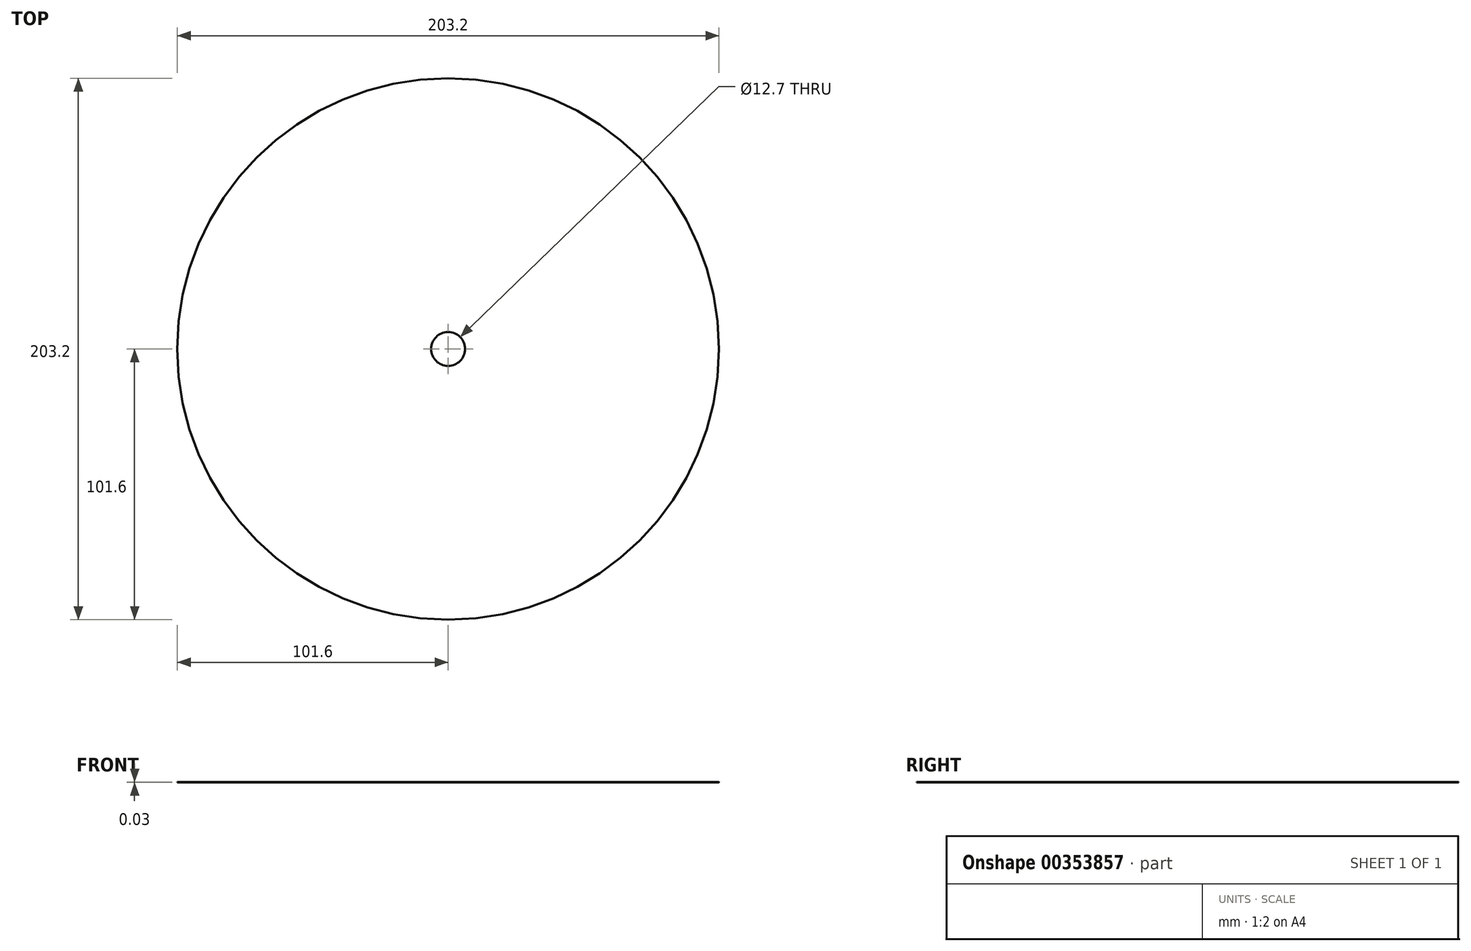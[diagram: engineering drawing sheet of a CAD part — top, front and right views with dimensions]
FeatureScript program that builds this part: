
annotation { "Feature Type Name" : "Feature", "Feature Type Description" : "" }
export const myFeature = defineFeature(function(context is Context, id is Id, definition is map)
    precondition{}
    {
        {
            var Q0;
            Q0=qCreatedBy(makeId("Top.planeOp"),FACE);
            var sketch = newSketch(context, id + "F0", { "sketchPlane" : qUnion([Q0])});
            skCircle(sketch, "E0", {"center": v(0, 0) * mm, "radius": 101.6 * mm});
            skSolve(sketch);
        }
        {
            var Q0;
            Q0 = qSketchRegion(id + "F0", true);
            extrude(context, id + "F1", {"entities" : qUnion([Q0]), "depth" : 3 / 101.6 * mm});
        }
        {
            var Q0;
            Q0=makeQuery(id+"F1.opExtrude","CAP_FACE",FACE,{"disambiguationData":[OSD([sQuery(id+"F0.wireOp",EDGE,"E0")])],"isStart":false});
            var sketch = newSketch(context, id + "F2", { "sketchPlane" : qUnion([Q0])});
            skCircle(sketch, "E1", {"center": v(0, 0) * mm, "radius": 6.35 * mm});
            skSolve(sketch);
        }
        {
            var Q0;
            Q0=makeQuery(id+"F2.imprint","IMPRINT",FACE,{"disambiguationData":[TD([[makeQuery(id+"F2.imprint","IMPRINT",EDGE,{"derivedFrom":sQuery(id+"F2.wireOp",EDGE,"E1")}),1.0]])]});
            extrude(context, id + "F3", {"entities" : qUnion([Q0]), "operationType" : NewBodyOperationType.REMOVE, "oppositeDirection" : true, "depth" : 6.35 * mm});
        }
    });
